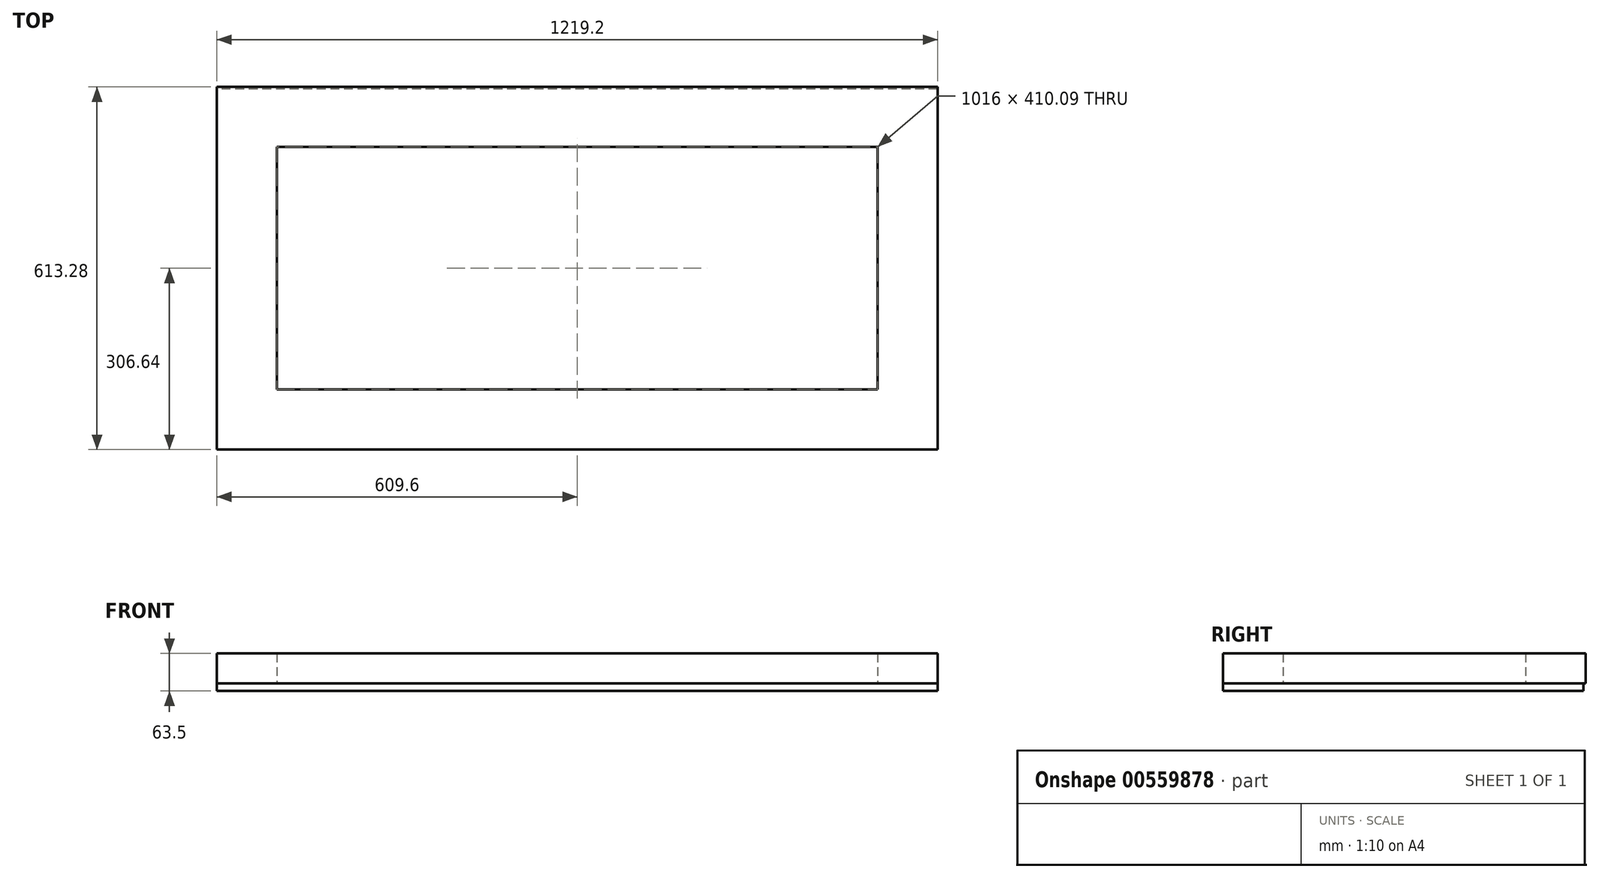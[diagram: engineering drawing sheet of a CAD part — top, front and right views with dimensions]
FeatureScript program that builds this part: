
annotation { "Feature Type Name" : "Feature", "Feature Type Description" : "" }
export const myFeature = defineFeature(function(context is Context, id is Id, definition is map)
    precondition{}
    {
        {
            var Q0;
            Q0=qCreatedBy(makeId("Top.planeOp"),FACE);
            var sketch = newSketch(context, id + "F0", { "sketchPlane" : qUnion([Q0])});
            skLineSegment(sketch, "E0.bottom", {"start": v(609.6, 302.96) * mm, "end": v(-609.6, 302.96) * mm});
            skLineSegment(sketch, "E0.top", {"start": v(609.6, -306.64) * mm, "end": v(-609.6, -306.64) * mm});
            skLineSegment(sketch, "E0.left", {"start": v(609.6, 302.96) * mm, "end": v(609.6, -306.64) * mm});
            skLineSegment(sketch, "E0.right", {"start": v(-609.6, 302.96) * mm, "end": v(-609.6, -306.64) * mm});
            skPoint(sketch, "E0.middle", {"position": v(0, -1.84) * mm});
            skSolve(sketch);
        }
        {
            var Q0;
            Q0 = qSketchRegion(id + "F0", true);
            extrude(context, id + "F1", {"entities" : qUnion([Q0]), "oppositeDirection" : true, "depth" : 12.7 * mm, "offsetDistance" : 25.4 * mm});
        }
        {
            var Q0;
            Q0=makeQuery(id+"F1.opExtrude","CAP_FACE",FACE,{"disambiguationData":[OSD([sQuery(id+"F0.wireOp",EDGE,"E0.bottom"),sQuery(id+"F0.wireOp",EDGE,"E0.top"),sQuery(id+"F0.wireOp",EDGE,"E0.left"),sQuery(id+"F0.wireOp",EDGE,"E0.right")])],"isStart":true});
            var sketch = newSketch(context, id + "F2", { "sketchPlane" : qUnion([Q0])});
            skLineSegment(sketch, "E1.bottom", {"start": v(-609.6, -306.64) * mm, "end": v(609.6, -306.64) * mm});
            skLineSegment(sketch, "E1.top", {"start": v(-609.6, -205.04) * mm, "end": v(609.6, -205.04) * mm});
            skLineSegment(sketch, "E1.left", {"start": v(-609.6, -306.64) * mm, "end": v(-609.6, -205.04) * mm});
            skLineSegment(sketch, "E1.right", {"start": v(609.6, -306.64) * mm, "end": v(609.6, -205.04) * mm});
            skLineSegment(sketch, "E2.MirrorCS", {"start": v(609.6, -306.64) * mm, "end": v(-609.6, -306.64) * mm});
            skLineSegment(sketch, "E3.MirrorCS", {"start": v(609.6, -205.04) * mm, "end": v(-609.6, -205.04) * mm});
            skLineSegment(sketch, "E4.MirrorCS", {"start": v(-609.6, 205.04) * mm, "end": v(609.6, 205.04) * mm});
            skLineSegment(sketch, "E5.MirrorCS", {"start": v(609.6, 306.64) * mm, "end": v(-609.6, 306.64) * mm});
            skLineSegment(sketch, "E6.MirrorCS", {"start": v(-609.6, 306.64) * mm, "end": v(-609.6, 205.04) * mm});
            skLineSegment(sketch, "E7.MirrorCS", {"start": v(609.6, 306.64) * mm, "end": v(609.6, 205.04) * mm});
            skLineSegment(sketch, "E8.bottom", {"start": v(-609.6, 205.04) * mm, "end": v(-508, 205.04) * mm});
            skLineSegment(sketch, "E8.top", {"start": v(-609.6, -205.04) * mm, "end": v(-508, -205.04) * mm});
            skLineSegment(sketch, "E8.left", {"start": v(-609.6, 205.04) * mm, "end": v(-609.6, -205.04) * mm});
            skLineSegment(sketch, "E8.right", {"start": v(-508, 205.04) * mm, "end": v(-508, -205.04) * mm});
            skLineSegment(sketch, "E9.MirrorCS", {"start": v(508, 205.04) * mm, "end": v(508, -205.04) * mm});
            skLineSegment(sketch, "E10.MirrorCS", {"start": v(609.6, 205.04) * mm, "end": v(609.6, -205.04) * mm});
            skSolve(sketch);
        }
        {
            var Q0;
            Q0 = qSketchRegion(id + "F2", true);
            extrude(context, id + "F3", {"entities" : qUnion([Q0]), "depth" : 50.8 * mm, "offsetDistance" : 25.4 * mm});
        }
    });
